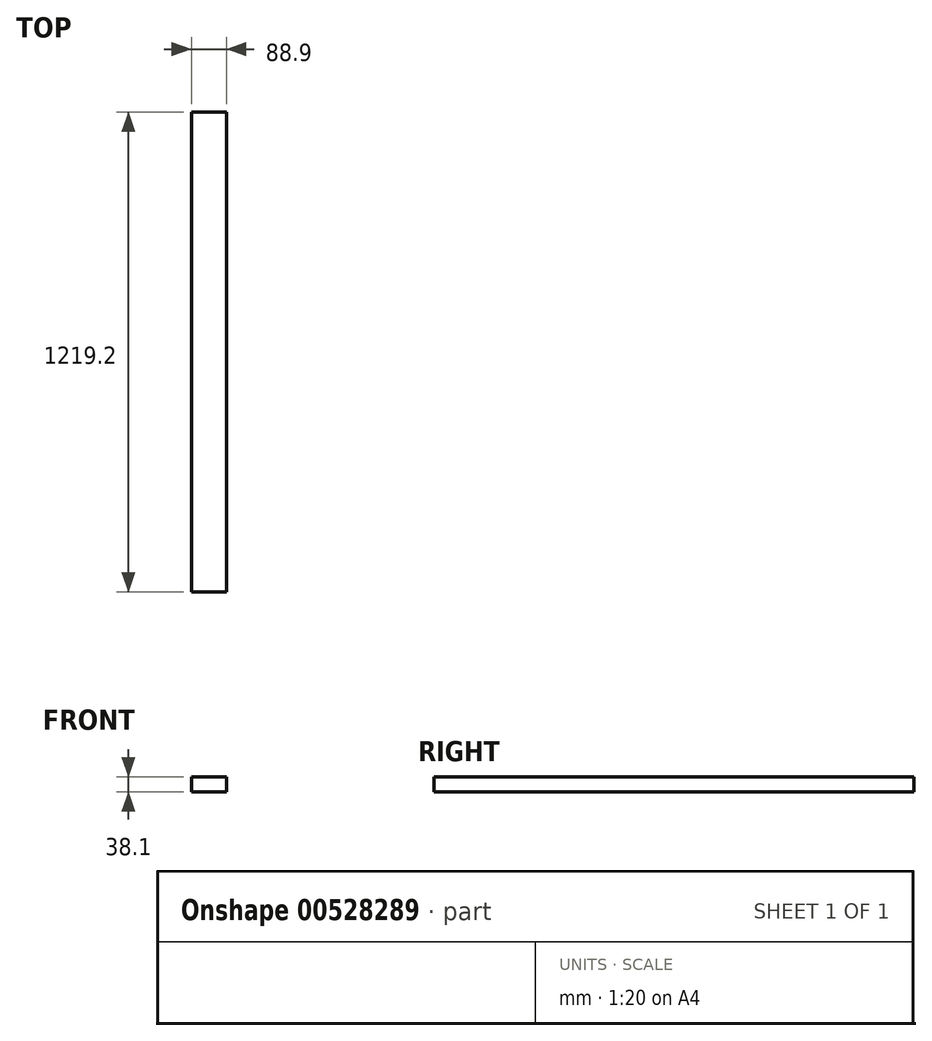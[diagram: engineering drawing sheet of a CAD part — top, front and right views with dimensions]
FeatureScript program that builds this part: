
annotation { "Feature Type Name" : "Feature", "Feature Type Description" : "" }
export const myFeature = defineFeature(function(context is Context, id is Id, definition is map)
    precondition{}
    {
        {
            var Q0;
            Q0=qCreatedBy(makeId("Right.planeOp"),FACE);
            var sketch = newSketch(context, id + "F0", { "sketchPlane" : qUnion([Q0])});
            skLineSegment(sketch, "E0", {"start": v(-283.91, 31.86) * mm, "end": v(935.29, 31.86) * mm});
            skLineSegment(sketch, "E1", {"start": v(935.29, 31.86) * mm, "end": v(935.29, -6.24) * mm});
            skLineSegment(sketch, "E2", {"start": v(935.29, -6.24) * mm, "end": v(-283.91, -6.24) * mm});
            skLineSegment(sketch, "E3", {"start": v(-283.91, -6.24) * mm, "end": v(-283.91, 31.86) * mm});
            skSolve(sketch);
        }
        {
            var Q0;
            Q0=makeQuery(id+"F0.imprint","IMPRINT",FACE,{"disambiguationData":[TD([[makeQuery(id+"F0.imprint","IMPRINT",EDGE,{"derivedFrom":sQuery(id+"F0.wireOp",EDGE,"E0")}),-1.0]])]});
            extrude(context, id + "F1", {"entities" : qUnion([Q0]), "depth" : 88.9 * mm, "offsetDistance" : 25.4 * mm});
        }
    });
